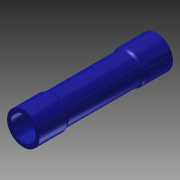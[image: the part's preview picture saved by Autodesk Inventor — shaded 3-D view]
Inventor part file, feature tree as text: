
AUTODESK INVENTOR PART (.ipt)
format: ipt  version: 2014 (Build 180170000, 170)  size: 164,352 bytes
history: native  units: in
note: dims shown in document units (in); Inventor stores cm internally (conversion verified against a paired STEP export)
features: sketch x3, extrude x2, fillet x2, projected_geometry x2, mirror x1, shell x1, revolve x1, chamfer x1
ambient origin geometry x8: Origin, YZ Plane, XZ Plane, XY Plane, X Axis, Y Axis, Z Axis, Center Point
bodies: Solid1 (feature_tree), Solid2 (feature_tree)
feature tree (13):
  extrude  "Extrusion1"  Depth=0.9735in TaperAngle=0.0deg
  extrude  "Extrusion2"  Depth=0.03in TaperAngle=0.0deg
  fillet  "Fillet1"  Radius=0.01in
  fillet  "Fillet2"  Radius=0.03in
  mirror  "Mirror1"
  shell  "Shell1"  Thickness=0.0285in
  revolve  "Revolution1"  [1 undecoded]
  chamfer  "Chamfer1"  Distance=0.03in
  sketch  "Sketch1"  dims[d0=0.217in d1=0.9735in d2=0.0in]
  sketch  "Sketch2"  dims[d3=0.237in d4=0.215in d5=0.0in d6=0.01in d7=0.03in d8=0.0285in]
  projected_geometry  "Projected Loop1"
  sketch  "Sketch3"  dims[d9=0.0265in d10=0.03in d11=0.03in d12=90.0deg d13=0.008in d14=0.125in d15=45.0deg]
  projected_geometry  "Project Cut Edges1"
note: 1 required parameter value undecoded (feature->parameter linkage not recoverable at this tier; creation-order binding heuristic only, values carry confidence <= 0.55)
